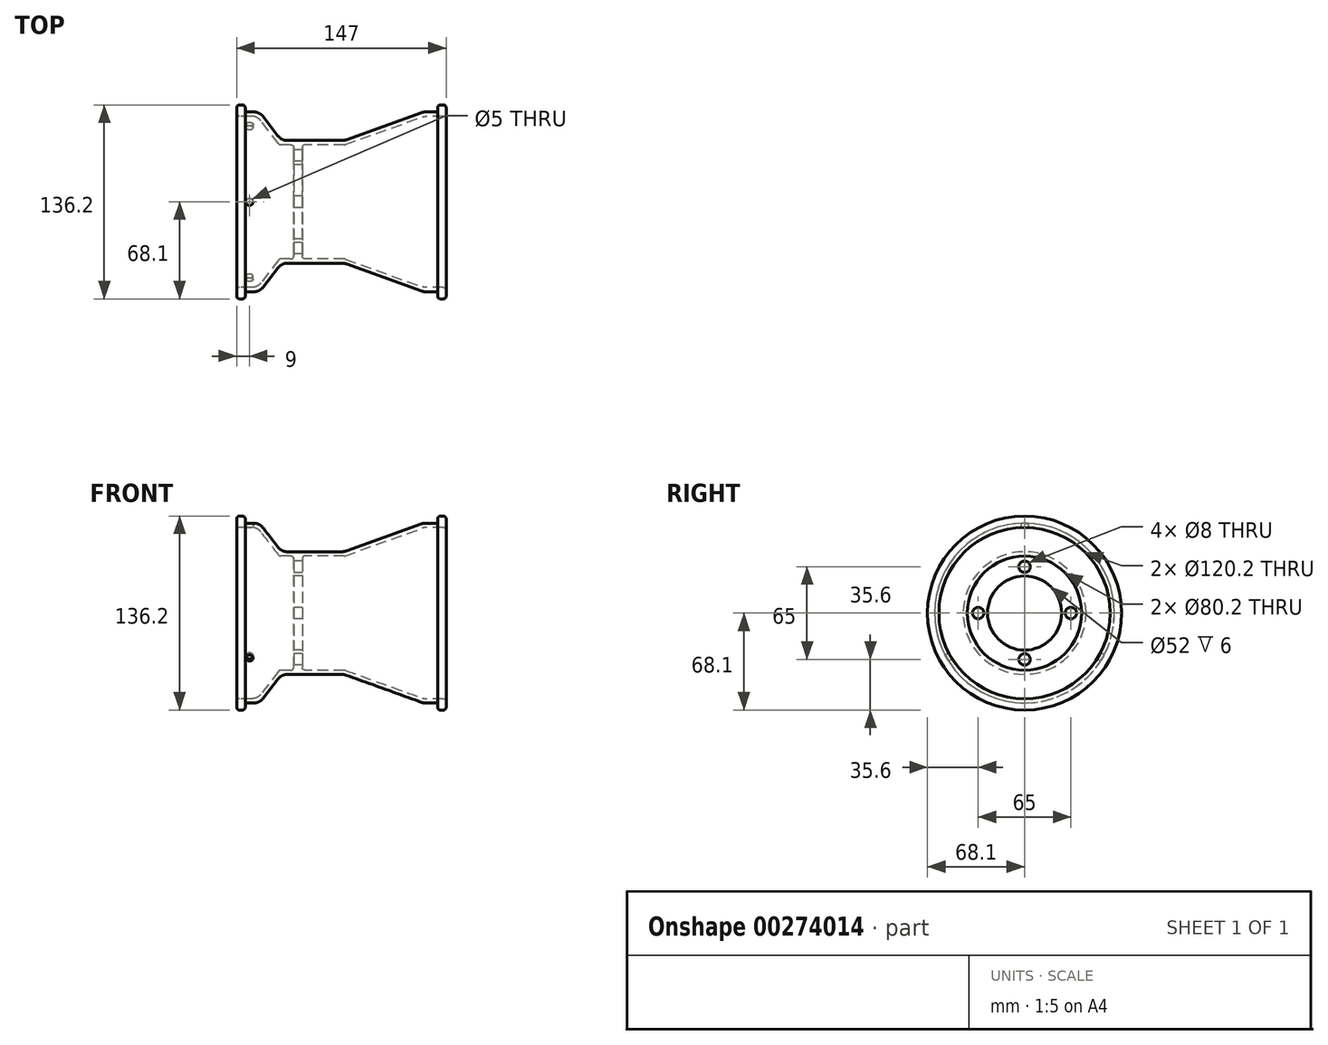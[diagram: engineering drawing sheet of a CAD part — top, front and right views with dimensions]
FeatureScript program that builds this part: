
annotation { "Feature Type Name" : "Feature", "Feature Type Description" : "" }
export const myFeature = defineFeature(function(context is Context, id is Id, definition is map)
    precondition{}
    {
        {
            var Q0;
            Q0=qCreatedBy(makeId("Front.planeOp"),FACE);
            var sketch = newSketch(context, id + "F0", { "sketchPlane" : qUnion([Q0])});
            skLineSegment(sketch, "E0", {"start": v(0, 0) * mm, "end": v(198.62, 0) * mm, "construction": true});
            skLineSegment(sketch, "E1", {"start": v(0, 68.1) * mm, "end": v(0, 60.1) * mm});
            skLineSegment(sketch, "E2", {"start": v(0, 60.1) * mm, "end": v(14.53, 60.1) * mm});
            skLineSegment(sketch, "E3", {"start": v(14.53, 60.1) * mm, "end": v(30, 40.1) * mm});
            skLineSegment(sketch, "E4", {"start": v(30, 40.1) * mm, "end": v(40, 40.1) * mm});
            skLineSegment(sketch, "E5", {"start": v(40, 40.1) * mm, "end": v(40, 0) * mm});
            skLineSegment(sketch, "E6", {"start": v(40, 0) * mm, "end": v(46, 0) * mm});
            skLineSegment(sketch, "E7", {"start": v(46, 0) * mm, "end": v(46, 40.1) * mm});
            skLineSegment(sketch, "E8", {"start": v(46, 40.1) * mm, "end": v(76, 40.1) * mm});
            skLineSegment(sketch, "E9", {"start": v(76, 40.1) * mm, "end": v(131.52, 60.1) * mm});
            skLineSegment(sketch, "E10", {"start": v(131.52, 60.1) * mm, "end": v(147, 60.1) * mm});
            skLineSegment(sketch, "E11", {"start": v(147, 60.1) * mm, "end": v(147, 68.1) * mm});
            skLineSegment(sketch, "E12", {"start": v(147, 68.1) * mm, "end": v(141, 68.1) * mm});
            skLineSegment(sketch, "E13", {"start": v(141, 68.1) * mm, "end": v(141, 63.1) * mm});
            skLineSegment(sketch, "E14", {"start": v(141, 63.1) * mm, "end": v(131, 63.1) * mm});
            skLineSegment(sketch, "E15", {"start": v(131, 63.1) * mm, "end": v(75.48, 43.1) * mm});
            skLineSegment(sketch, "E16", {"start": v(75.48, 43.1) * mm, "end": v(31.47, 43.1) * mm});
            skLineSegment(sketch, "E17", {"start": v(31.47, 43.1) * mm, "end": v(16, 63.1) * mm});
            skLineSegment(sketch, "E18", {"start": v(16, 63.1) * mm, "end": v(6, 63.1) * mm});
            skLineSegment(sketch, "E19", {"start": v(6, 63.1) * mm, "end": v(6, 68.1) * mm});
            skLineSegment(sketch, "E20", {"start": v(6, 68.1) * mm, "end": v(0, 68.1) * mm});
            skSolve(sketch);
        }
        {
            var Q0;
            Q0=makeQuery(id+"F0.imprint","IMPRINT",FACE,{"disambiguationData":[TD([[makeQuery(id+"F0.imprint","IMPRINT",EDGE,{"derivedFrom":sQuery(id+"F0.wireOp",EDGE,"E1")}),1.0]])]});
            var Q1;
            Q1=sQuery(id+"F0.wireOp",EDGE,"E0");
            revolve(context, id + "F1", {"entities" : qUnion([Q0]), "axis" : qUnion([Q1]), "revolveType" : RevolveType.FULL});
        }
        {
            var Q0;
            Q0=makeQuery(id+"F1.opRevolve","SWEPT_EDGE",EDGE,{"disambiguationData":[OSD([sQuery(id+"F0.wireOp",EDGE,"E17"),sQuery(id+"F0.wireOp",EDGE,"E18")])]});
            var Q1;
            Q1=makeQuery(id+"F1.opRevolve","SWEPT_EDGE",EDGE,{"disambiguationData":[OSD([sQuery(id+"F0.wireOp",EDGE,"E14"),sQuery(id+"F0.wireOp",EDGE,"E15")])]});
            var Q2;
            Q2=makeQuery(id+"F1.opRevolve","SWEPT_EDGE",EDGE,{"disambiguationData":[OSD([sQuery(id+"F0.wireOp",EDGE,"E15"),sQuery(id+"F0.wireOp",EDGE,"E16")])]});
            var Q3;
            Q3=makeQuery(id+"F1.opRevolve","SWEPT_EDGE",EDGE,{"disambiguationData":[OSD([sQuery(id+"F0.wireOp",EDGE,"E16"),sQuery(id+"F0.wireOp",EDGE,"E17")])]});
            var Q4;
            Q4=makeQuery(id+"F1.opRevolve","SWEPT_EDGE",EDGE,{"disambiguationData":[OSD([sQuery(id+"F0.wireOp",EDGE,"E2"),sQuery(id+"F0.wireOp",EDGE,"E3")])]});
            var Q5;
            Q5=makeQuery(id+"F1.opRevolve","SWEPT_EDGE",EDGE,{"disambiguationData":[OSD([sQuery(id+"F0.wireOp",EDGE,"E9"),sQuery(id+"F0.wireOp",EDGE,"E10")])]});
            fillet(context, id + "F2", {"entities" : qUnion([Q0, Q1, Q2, Q3, Q4, Q5]), "radius" : 8 * mm, "tangentPropagation" : true, "allowEdgeOverflow" : false});
        }
        {
            var Q0;
            Q0=makeQuery(id+"F1.opRevolve","SWEPT_EDGE",EDGE,{"disambiguationData":[OSD([sQuery(id+"F0.wireOp",EDGE,"E1"),sQuery(id+"F0.wireOp",EDGE,"E20")])]});
            var Q1;
            Q1=makeQuery(id+"F1.opRevolve","SWEPT_EDGE",EDGE,{"disambiguationData":[OSD([sQuery(id+"F0.wireOp",EDGE,"E19"),sQuery(id+"F0.wireOp",EDGE,"E20")])]});
            var Q2;
            Q2=makeQuery(id+"F1.opRevolve","SWEPT_EDGE",EDGE,{"disambiguationData":[OSD([sQuery(id+"F0.wireOp",EDGE,"E12"),sQuery(id+"F0.wireOp",EDGE,"E13")])]});
            var Q3;
            Q3=makeQuery(id+"F1.opRevolve","SWEPT_EDGE",EDGE,{"disambiguationData":[OSD([sQuery(id+"F0.wireOp",EDGE,"E11"),sQuery(id+"F0.wireOp",EDGE,"E12")])]});
            var Q4;
            Q4=makeQuery(id+"F1.opRevolve","SWEPT_EDGE",EDGE,{"disambiguationData":[OSD([sQuery(id+"F0.wireOp",EDGE,"E1"),sQuery(id+"F0.wireOp",EDGE,"E2")])]});
            var Q5;
            Q5=makeQuery(id+"F1.opRevolve","SWEPT_EDGE",EDGE,{"disambiguationData":[OSD([sQuery(id+"F0.wireOp",EDGE,"E3"),sQuery(id+"F0.wireOp",EDGE,"E4")])]});
            var Q6;
            Q6=makeQuery(id+"F1.opRevolve","SWEPT_EDGE",EDGE,{"disambiguationData":[OSD([sQuery(id+"F0.wireOp",EDGE,"E10"),sQuery(id+"F0.wireOp",EDGE,"E11")])]});
            var Q7;
            Q7=makeQuery(id+"F1.opRevolve","SWEPT_EDGE",EDGE,{"disambiguationData":[OSD([sQuery(id+"F0.wireOp",EDGE,"E7"),sQuery(id+"F0.wireOp",EDGE,"E8")])]});
            var Q8;
            Q8=makeQuery(id+"F1.opRevolve","SWEPT_EDGE",EDGE,{"disambiguationData":[OSD([sQuery(id+"F0.wireOp",EDGE,"E8"),sQuery(id+"F0.wireOp",EDGE,"E9")])]});
            var Q9;
            Q9=makeQuery(id+"F1.opRevolve","SWEPT_EDGE",EDGE,{"disambiguationData":[OSD([sQuery(id+"F0.wireOp",EDGE,"E4"),sQuery(id+"F0.wireOp",EDGE,"E5")])]});
            fillet(context, id + "F3", {"entities" : qUnion([Q0, Q1, Q2, Q3, Q4, Q5, Q6, Q7, Q8, Q9]), "radius" : 2 * mm, "tangentPropagation" : true, "allowEdgeOverflow" : false});
        }
        {
            var Q0;
            Q0=makeQuery(id+"F1.opRevolve","SWEPT_FACE",FACE,{"disambiguationData":[OSD([sQuery(id+"F0.wireOp",EDGE,"E5")])]});
            var sketch = newSketch(context, id + "F4", { "sketchPlane" : qUnion([Q0])});
            skCircle(sketch, "E21", {"center": v(0, 0) * mm, "radius": 32.5 * mm, "construction": true});
            skCircle(sketch, "E22", {"center": v(0, 32.5) * mm, "radius": 4 * mm});
            skCircle(sketch, "E23", {"center": v(32.5, 0) * mm, "radius": 4 * mm});
            skCircle(sketch, "E24", {"center": v(0, -32.5) * mm, "radius": 4 * mm});
            skCircle(sketch, "E25", {"center": v(-32.5, 0) * mm, "radius": 4 * mm});
            skCircle(sketch, "E26", {"center": v(0, 0) * mm, "radius": 26 * mm});
            skSolve(sketch);
        }
        {
            var Q0;
            Q0=qSketchRegion(id+"F4",true);
            extrude(context, id + "F5", {"entities" : qUnion([Q0]), "operationType" : NewBodyOperationType.REMOVE, "endBound" : BoundingType.THROUGH_ALL, "oppositeDirection" : true, "depth" : 25 * mm});
        }
        {
            var Q0;
            Q0=qCreatedBy(makeId("Top.planeOp"),FACE);
            var sketch = newSketch(context, id + "F6", { "sketchPlane" : qUnion([Q0])});
            skCircle(sketch, "E27", {"center": v(9, 0) * mm, "radius": 2.5 * mm});
            skSolve(sketch);
        }
        {
            var Q0;
            Q0=qSketchRegion(id+"F6",true);
            extrude(context, id + "F7", {"entities" : qUnion([Q0]), "operationType" : NewBodyOperationType.REMOVE, "endBound" : BoundingType.THROUGH_ALL, "depth" : 25 * mm});
        }
        {
            var Q0;
            Q0=makeQuery(id+"F7.boolean.opBoolean","COPY",FACE,{"derivedFrom":makeQuery(id+"F7.opExtrude","SWEPT_FACE",FACE,{"disambiguationData":[OSD([sQuery(id+"F6.wireOp",EDGE,"E27")])]})});
            var Q1;
            Q1=makeQuery(id+"F5.boolean.opBoolean","COPY",FACE,{"derivedFrom":makeQuery(id+"F5.opExtrude","SWEPT_FACE",FACE,{"disambiguationData":[OSD([sQuery(id+"F4.wireOp",EDGE,"E26")])]})});
            circularPattern(context, id + "F8", {"faces" : qUnion([Q0]), "axis" : qUnion([Q1]), "angle" : 360 * degree, "instanceCount" : 3, "equalSpace" : true, "patternType" : PatternType.FACE});
        }
    });
